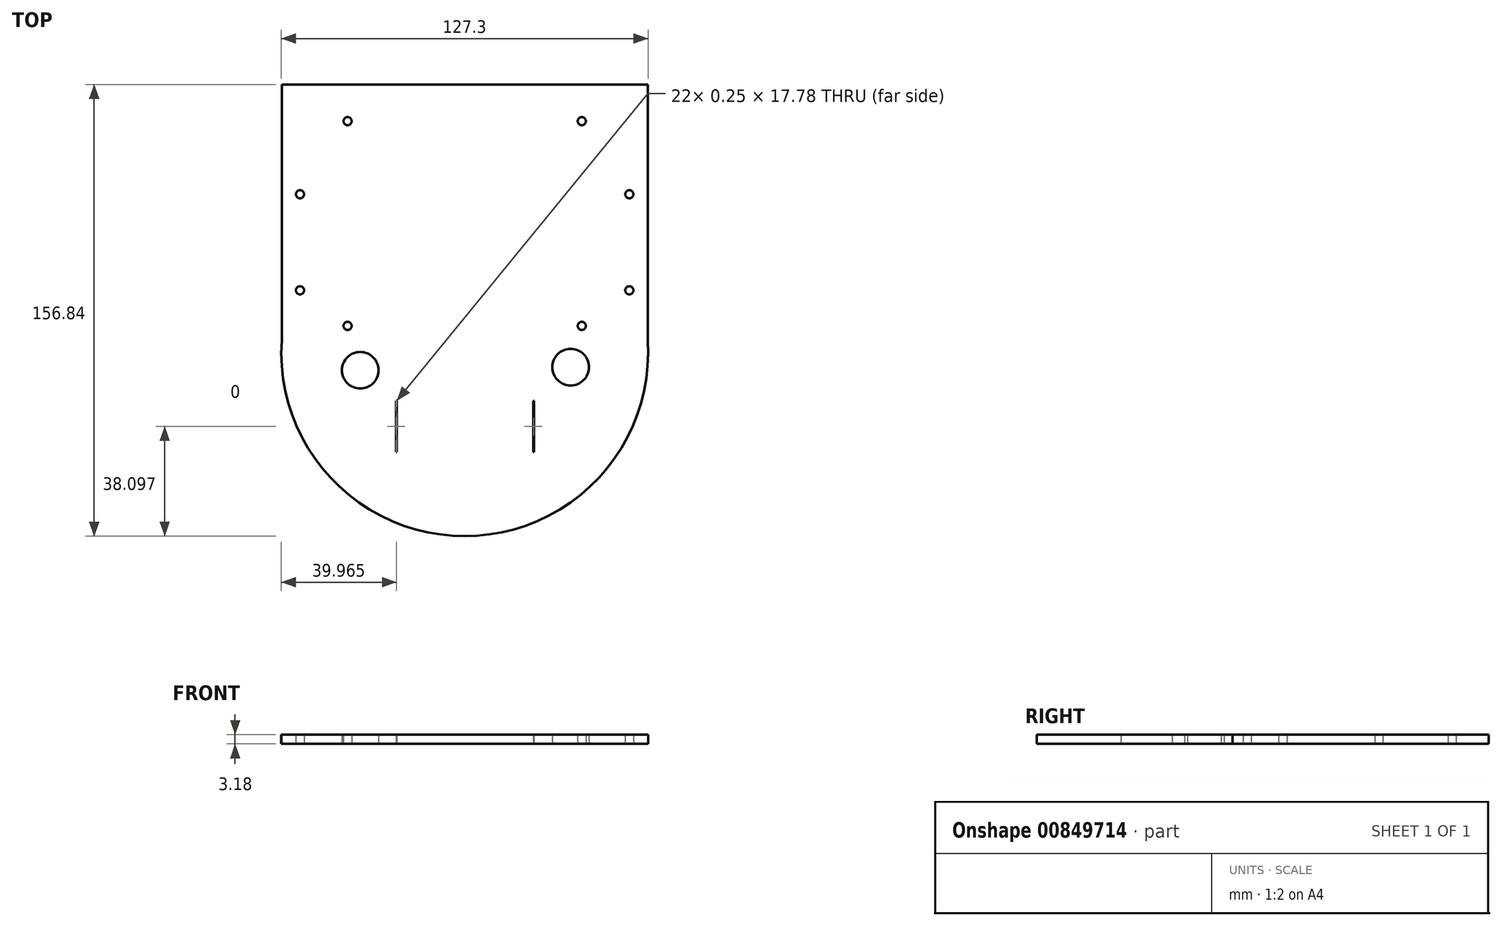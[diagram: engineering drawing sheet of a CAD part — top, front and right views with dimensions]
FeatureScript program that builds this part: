
annotation { "Feature Type Name" : "Feature", "Feature Type Description" : "" }
export const myFeature = defineFeature(function(context is Context, id is Id, definition is map)
    precondition{}
    {
        {
            var Q0;
            Q0=qCreatedBy(makeId("Top.planeOp"),FACE);
            var sketch = newSketch(context, id + "F0", { "sketchPlane" : qUnion([Q0])});
            skLineSegment(sketch, "E0.bottom", {"start": v(63.5, 88.9) * mm, "end": v(-63.5, 88.9) * mm});
            skLineSegment(sketch, "E0.left", {"start": v(63.5, 88.9) * mm, "end": v(63.5, -8.6) * mm});
            skLineSegment(sketch, "E0.right", {"start": v(-63.5, 88.9) * mm, "end": v(-63.5, -8.6) * mm});
            skPoint(sketch, "E0.middle", {"position": v(0, 0) * mm});
            skCircle(sketch, "E1", {"center": v(-57.15, 50.8) * mm, "radius": 1.42 * mm});
            skCircle(sketch, "E2", {"center": v(-57.15, 17.45) * mm, "radius": 1.42 * mm});
            skCircle(sketch, "E3.1.0.0", {"center": v(57.15, 17.45) * mm, "radius": 1.42 * mm});
            skCircle(sketch, "E3.1.0.2", {"center": v(57.15, 50.8) * mm, "radius": 1.42 * mm});
            skLineSegment(sketch, "E4", {"start": v(0, 88.9) * mm, "end": v(0, 88.9) * mm});
            skCircle(sketch, "E5", {"center": v(-40.64, 76.2) * mm, "radius": 1.42 * mm});
            skLineSegment(sketch, "E6.left", {"start": v(23.81, -20.95) * mm, "end": v(23.81, -38.73) * mm});
            skLineSegment(sketch, "E6.right", {"start": v(-23.81, -20.95) * mm, "end": v(-23.81, -38.73) * mm});
            skArc(sketch, "E7", {"start": v(-63.5, 0) * mm, "mid": v(0, -67.94) * mm, "end": v(63.5, 0) * mm});
            skPoint(sketch, "E8.orphan", {"position": v(-63.5, -88.9) * mm});
            skPoint(sketch, "E9.orphan", {"position": v(63.5, -88.9) * mm});
            skCircle(sketch, "E10.0.1.0", {"center": v(-40.64, 5.08) * mm, "radius": 1.42 * mm});
            skCircle(sketch, "E10.1.0.0", {"center": v(40.64, 76.2) * mm, "radius": 1.42 * mm});
            skCircle(sketch, "E10.1.1.0", {"center": v(40.64, 5.08) * mm, "radius": 1.42 * mm});
            skLineSegment(sketch, "E10.direction1", {"start": v(-40.64, 76.2) * mm, "end": v(40.64, 76.2) * mm, "construction": true});
            skLineSegment(sketch, "E10.direction2", {"start": v(-40.64, 76.2) * mm, "end": v(-40.64, 5.08) * mm, "construction": true});
            skLineSegment(sketch, "E11", {"start": v(-23.81, -20.95) * mm, "end": v(-23.56, -20.95) * mm});
            skLineSegment(sketch, "E12", {"start": v(-23.56, -20.95) * mm, "end": v(-23.56, -38.73) * mm});
            skLineSegment(sketch, "E13", {"start": v(-23.56, -38.73) * mm, "end": v(-23.81, -38.73) * mm});
            skLineSegment(sketch, "E14", {"start": v(23.81, -20.95) * mm, "end": v(24.07, -20.95) * mm});
            skLineSegment(sketch, "E15", {"start": v(24.07, -20.95) * mm, "end": v(24.07, -38.73) * mm});
            skLineSegment(sketch, "E16", {"start": v(24.07, -38.73) * mm, "end": v(23.81, -38.73) * mm});
            skCircle(sketch, "E17", {"center": v(36.77, -9.24) * mm, "radius": 6.35 * mm});
            skCircle(sketch, "E18", {"center": v(-36.26, -10.33) * mm, "radius": 6.35 * mm});
            skSolve(sketch);
        }
        {
            var Q0;
            Q0 = qSketchRegion(id + "F0", true);
            extrude(context, id + "F1", {"entities" : qUnion([Q0]), "depth" : 3.17 * mm, "offsetDistance" : 25.4 * mm});
        }
    });
